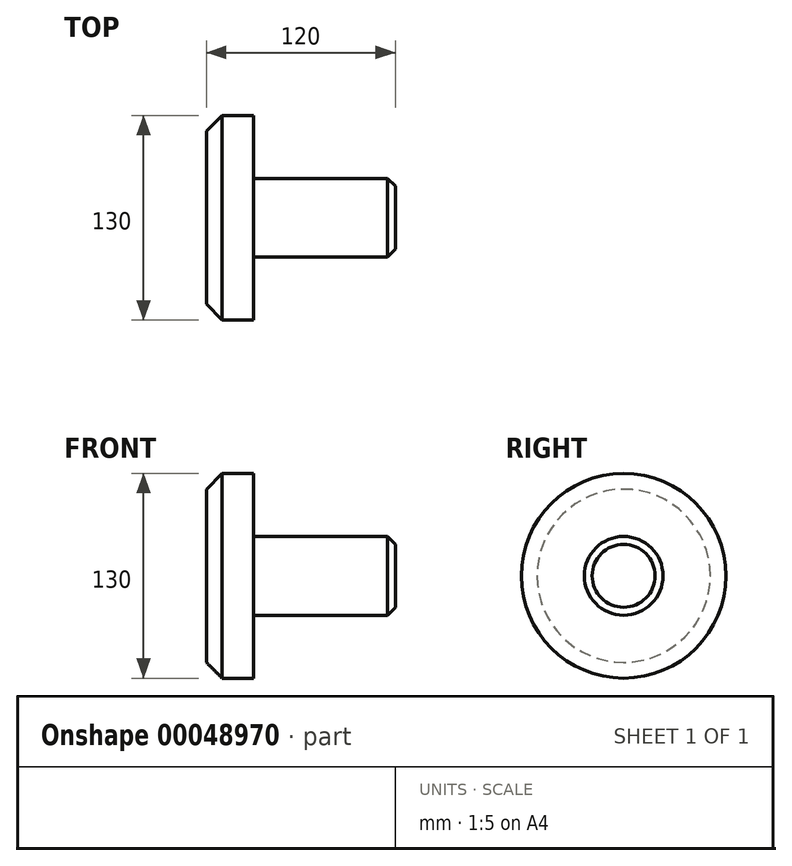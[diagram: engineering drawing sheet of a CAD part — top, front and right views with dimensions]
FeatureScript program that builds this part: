
annotation { "Feature Type Name" : "Feature", "Feature Type Description" : "" }
export const myFeature = defineFeature(function(context is Context, id is Id, definition is map)
    precondition{}
    {
        {
            var Q0;
            Q0=qCreatedBy(makeId("Top.planeOp"),FACE);
            var sketch = newSketch(context, id + "F0", { "sketchPlane" : qUnion([Q0])});
            skLineSegment(sketch, "E0", {"start": v(0, 0) * mm, "end": v(0, 65) * mm});
            skLineSegment(sketch, "E1", {"start": v(0, 65) * mm, "end": v(30, 65) * mm});
            skLineSegment(sketch, "E2", {"start": v(30, 65) * mm, "end": v(30, 25) * mm});
            skLineSegment(sketch, "E3", {"start": v(30, 25) * mm, "end": v(120, 25) * mm});
            skLineSegment(sketch, "E4", {"start": v(120, 25) * mm, "end": v(120, 0) * mm});
            skLineSegment(sketch, "E5", {"start": v(120, 0) * mm, "end": v(0, 0) * mm});
            skLineSegment(sketch, "E6", {"start": v(30, 25) * mm, "end": v(102, 25) * mm});
            skSolve(sketch);
        }
        {
            var Q0;
            Q0=makeQuery(id+"F0.imprint","IMPRINT",FACE,{"disambiguationData":[TD([[makeQuery(id+"F0.imprint","IMPRINT",EDGE,{"derivedFrom":sQuery(id+"F0.wireOp",EDGE,"E0")}),-1.0]])]});
            var Q1;
            Q1=sQuery(id+"F0.wireOp",EDGE,"E5");
            revolve(context, id + "F1", {"entities" : qUnion([Q0]), "axis" : qUnion([Q1]), "revolveType" : RevolveType.FULL});
        }
        {
            var Q0;
            Q0=makeQuery(id+"F1.opRevolve","SWEPT_EDGE",EDGE,{"disambiguationData":[OSD([sQuery(id+"F0.wireOp",EDGE,"E0"),sQuery(id+"F0.wireOp",EDGE,"E1")])]});
            chamfer(context, id + "F2", {"entities" : qUnion([Q0]), "chamferType" : ChamferType.OFFSET_ANGLE, "width" : 10 * mm, "oppositeDirection" : false, "angle" : 45 * degree, "tangentPropagation" : true});
        }
        {
            var Q0;
            Q0=makeQuery(id+"F1.opRevolve","SWEPT_EDGE",EDGE,{"disambiguationData":[OSD([sQuery(id+"F0.wireOp",EDGE,"E3"),sQuery(id+"F0.wireOp",EDGE,"E4")])]});
            chamfer(context, id + "F3", {"entities" : qUnion([Q0]), "width" : 5 * mm, "tangentPropagation" : true});
        }
    });
